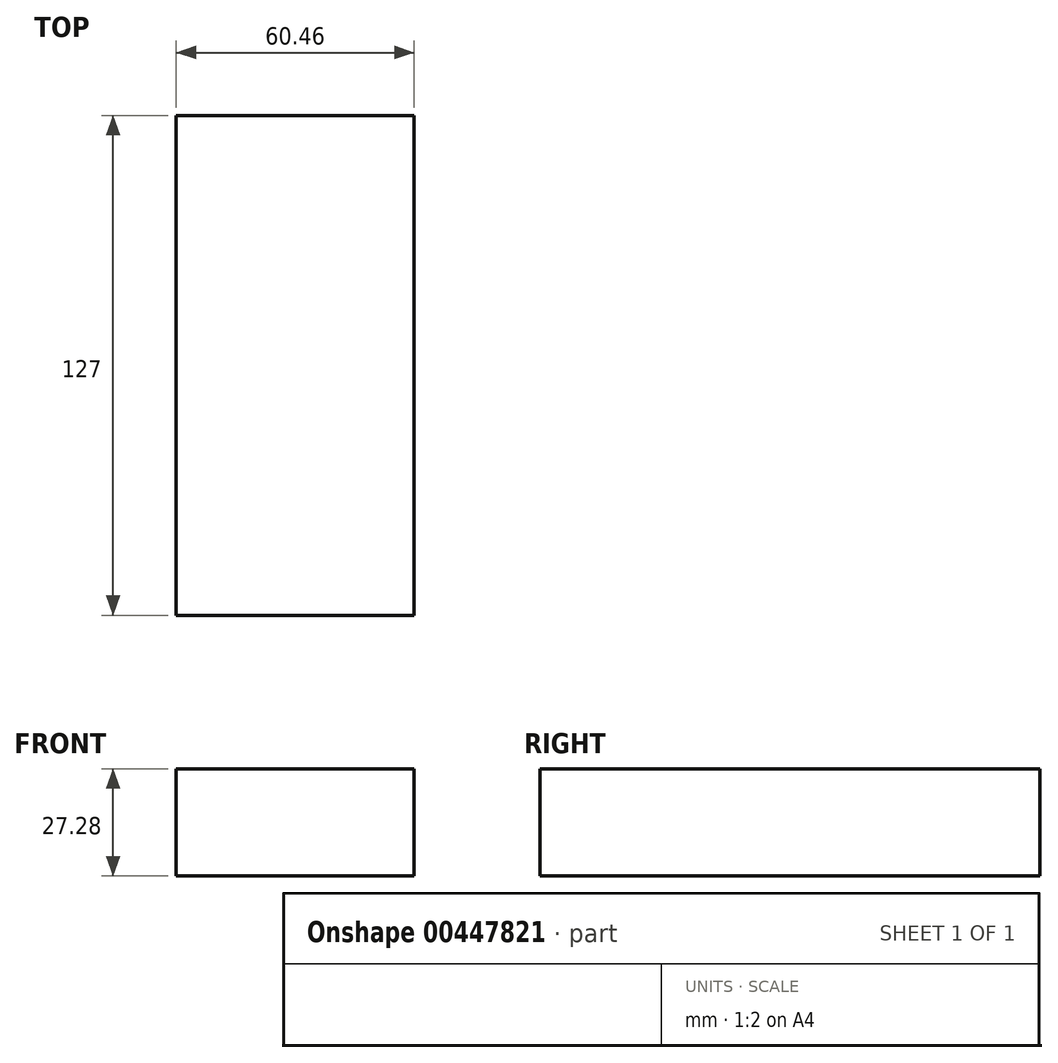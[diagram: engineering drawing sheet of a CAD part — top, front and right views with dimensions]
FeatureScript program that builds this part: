
annotation { "Feature Type Name" : "Feature", "Feature Type Description" : "" }
export const myFeature = defineFeature(function(context is Context, id is Id, definition is map)
    precondition{}
    {
        {
            var Q0;
            Q0=qCreatedBy(makeId("Front.planeOp"),FACE);
            var sketch = newSketch(context, id + "F0", { "sketchPlane" : qUnion([Q0])});
            skLineSegment(sketch, "E0.bottom", {"start": v(-30.23, 13.64) * mm, "end": v(30.23, 13.64) * mm});
            skLineSegment(sketch, "E0.top", {"start": v(-30.23, -13.64) * mm, "end": v(30.23, -13.64) * mm});
            skLineSegment(sketch, "E0.left", {"start": v(-30.23, 13.64) * mm, "end": v(-30.23, -13.64) * mm});
            skLineSegment(sketch, "E0.right", {"start": v(30.23, 13.64) * mm, "end": v(30.23, -13.64) * mm});
            skPoint(sketch, "E0.middle", {"position": v(0, 0) * mm});
            skSolve(sketch);
        }
        {
            var Q0;
            Q0=makeQuery(id+"F0.imprint","IMPRINT",FACE,{"disambiguationData":[TD([[makeQuery(id+"F0.imprint","IMPRINT",EDGE,{"derivedFrom":sQuery(id+"F0.wireOp",EDGE,"E0.bottom")}),-1.0]])]});
            extrude(context, id + "F1", {"entities" : qUnion([Q0]), "depth" : 63.5 * mm, "hasSecondDirection" : true, "secondDirectionOppositeDirection" : true, "secondDirectionDepth" : 63.5 * mm});
        }
    });
